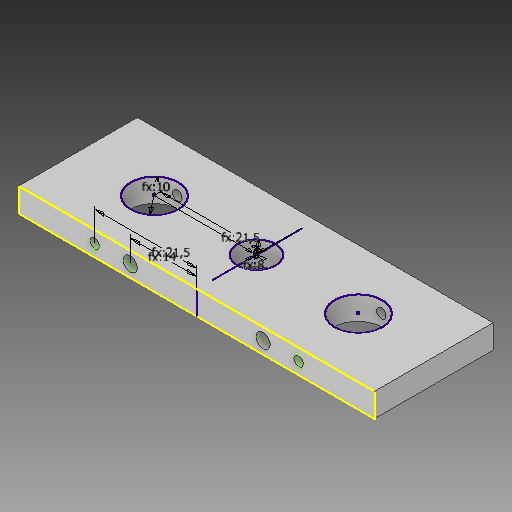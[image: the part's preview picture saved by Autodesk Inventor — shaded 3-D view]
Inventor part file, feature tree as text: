
AUTODESK INVENTOR PART (.ipt)
format: ipt  version: 2017 (Build 210142000, 142)  size: 134,144 bytes
history: native  units: mm
features: sketch x3, extrude x2, hole x2, other x1, projected_geometry x1
ambient origin geometry x8: Origin, YZ Plane, XZ Plane, XY Plane, X Axis, Y Axis, Z Axis, Center Point
bodies: Body1 (feature_tree)
feature tree (9):
  other  "Sólido1"
  extrude  "Extrusión1"  Depth=5.0mm
  sketch  "Boceto2"  dims[d5=75.0mm d12=14.0mm]
  hole  "Agujero1"  [1 undecoded]
  hole  "Agujero2"  [1 undecoded]
  extrude  "Extrusión2"  TaperAngle=0.0deg  [1 undecoded]
  sketch  "Boceto1"  dims[d2=5.0mm d3=0.0mm d4=25.0mm]
  projected_geometry  "Contorno proyectado1"
  sketch  "Boceto3"  dims[d13=21.5mm d14=3.0mm d15=6.0mm d16=4.0mm d17=2.0mm d18=90.0deg d19=8.0mm d20=20.594885mm d21=2.0mm d22=6.0mm d23=4.0mm d24=2.0mm d25=90.0deg d26=20.0mm d27=20.594885mm d28=21.5mm d29=0.0mm d30=10.0mm d31=0.0mm d32=5.0mm d33=0.0mm d34=8.0mm d35=0.0mm d36=0.0mm]
note: 3 required parameter values undecoded (feature->parameter linkage not recoverable at this tier; creation-order binding heuristic only, values carry confidence <= 0.55)
